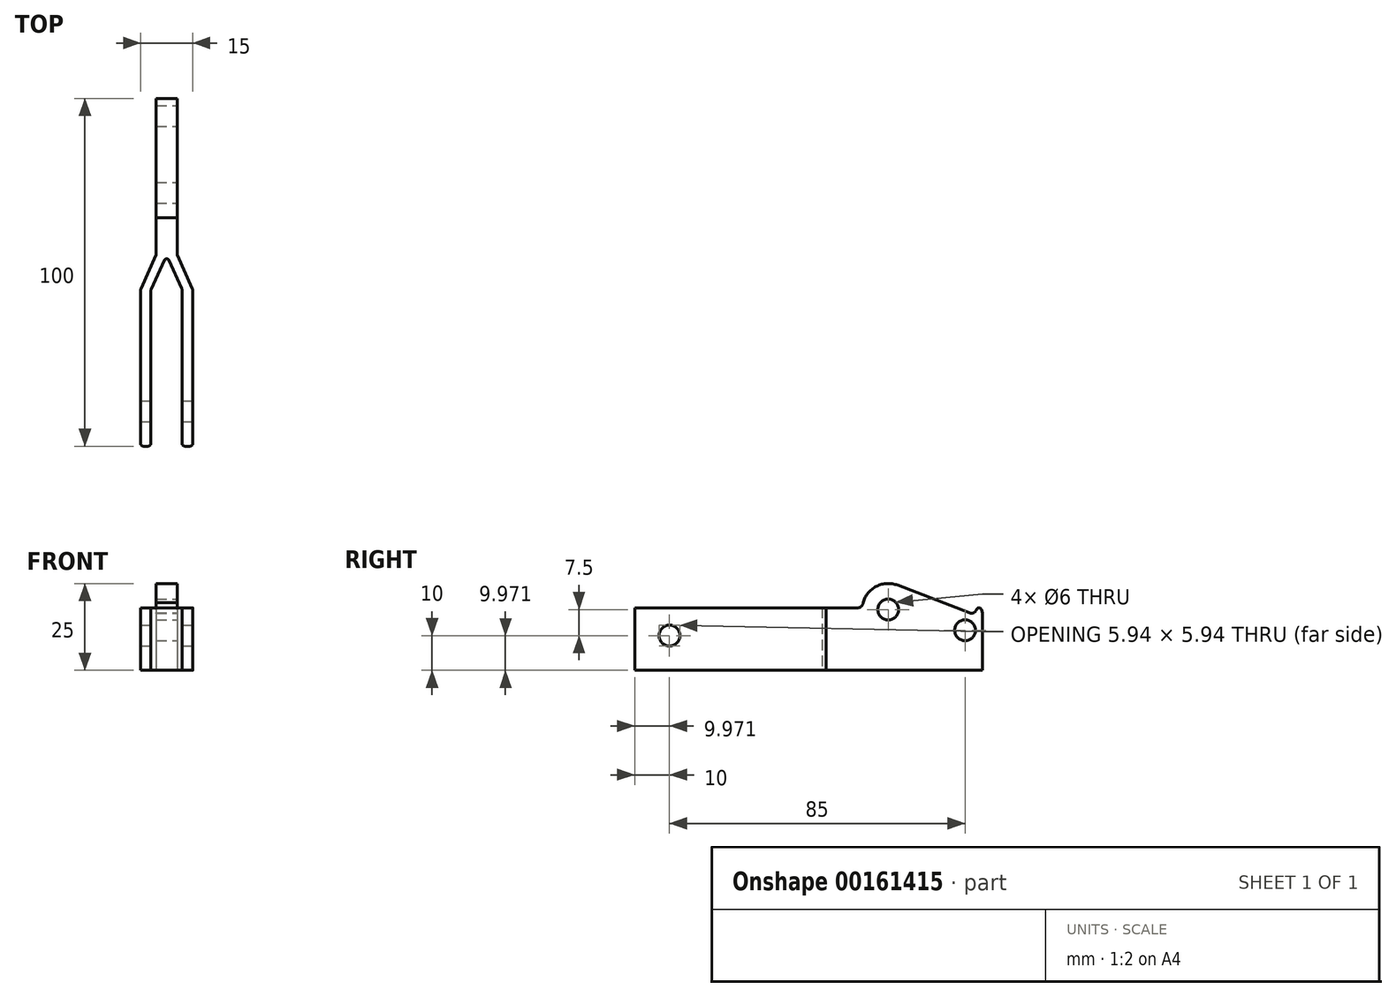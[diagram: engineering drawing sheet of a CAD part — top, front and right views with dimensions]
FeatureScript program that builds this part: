
annotation { "Feature Type Name" : "Feature", "Feature Type Description" : "" }
export const myFeature = defineFeature(function(context is Context, id is Id, definition is map)
    precondition{}
    {
        {
            var Q0;
            Q0=qCreatedBy(makeId("Top.planeOp"),FACE);
            var sketch = newSketch(context, id + "F0", { "sketchPlane" : qUnion([Q0])});
            skLineSegment(sketch, "E0.top", {"start": v(6.75, -22.5) * mm, "end": v(5.18, -22.5) * mm});
            skLineSegment(sketch, "E0.left", {"start": v(7.5, 22.18) * mm, "end": v(7.5, -21.75) * mm});
            skLineSegment(sketch, "E0.right", {"start": v(-7.5, 22.18) * mm, "end": v(-7.5, -21.75) * mm});
            skPoint(sketch, "E0.middle", {"position": v(0, 0) * mm});
            skLineSegment(sketch, "E1.left", {"start": v(-4.57, -21.75) * mm, "end": v(-4.57, 22.03) * mm});
            skLineSegment(sketch, "E1.right", {"start": v(4.43, -21.75) * mm, "end": v(4.43, 22.32) * mm});
            skLineSegment(sketch, "E2.trimOffspring", {"start": v(-5.32, -22.5) * mm, "end": v(-6.75, -22.5) * mm});
            skPoint(sketch, "E3", {"position": v(0, 32.5) * mm});
            skLineSegment(sketch, "E4", {"start": v(-4.43, 22.65) * mm, "end": v(-0.68, 30.98) * mm});
            skLineSegment(sketch, "E5", {"start": v(4.3, 22.94) * mm, "end": v(0.68, 30.98) * mm});
            skLineSegment(sketch, "E6", {"start": v(-7.37, 22.8) * mm, "end": v(-3, 32.5) * mm});
            skLineSegment(sketch, "E7", {"start": v(7.37, 22.8) * mm, "end": v(3, 32.5) * mm});
            skLineSegment(sketch, "E8.top", {"start": v(3, 77.5) * mm, "end": v(-3, 77.5) * mm});
            skLineSegment(sketch, "E8.left", {"start": v(3, 32.5) * mm, "end": v(3, 77.5) * mm});
            skLineSegment(sketch, "E8.right", {"start": v(-3, 32.5) * mm, "end": v(-3, 77.5) * mm});
            skPoint(sketch, "E8.middle", {"position": v(0, 55) * mm});
            skArc(sketch, "E9.filletArc", {"start": v(0.68, 30.98) * mm, "mid": v(0, 31.42) * mm, "end": v(-0.68, 30.98) * mm});
            skPoint(sketch, "E10.visualSharp", {"position": v(-4.57, -22.5) * mm});
            skArc(sketch, "E10.filletArc", {"start": v(-5.32, -22.5) * mm, "mid": v(-4.79, -22.28) * mm, "end": v(-4.57, -21.75) * mm});
            skPoint(sketch, "E11.visualSharp", {"position": v(-7.5, -22.5) * mm});
            skArc(sketch, "E11.filletArc", {"start": v(-7.5, -21.75) * mm, "mid": v(-7.28, -22.28) * mm, "end": v(-6.75, -22.5) * mm});
            skPoint(sketch, "E12.visualSharp", {"position": v(4.43, -22.5) * mm});
            skArc(sketch, "E12.filletArc", {"start": v(4.43, -21.75) * mm, "mid": v(4.65, -22.28) * mm, "end": v(5.18, -22.5) * mm});
            skPoint(sketch, "E13.visualSharp", {"position": v(7.5, -22.5) * mm});
            skArc(sketch, "E13.filletArc", {"start": v(6.75, -22.5) * mm, "mid": v(7.28, -22.28) * mm, "end": v(7.5, -21.75) * mm});
            skPoint(sketch, "E14.visualSharp", {"position": v(-4.57, 22.35) * mm});
            skArc(sketch, "E14.filletArc", {"start": v(-4.43, 22.65) * mm, "mid": v(-4.53, 22.35) * mm, "end": v(-4.57, 22.03) * mm});
            skPoint(sketch, "E15.visualSharp", {"position": v(4.43, 22.65) * mm});
            skArc(sketch, "E15.filletArc", {"start": v(4.43, 22.32) * mm, "mid": v(4.4, 22.64) * mm, "end": v(4.3, 22.94) * mm});
            skPoint(sketch, "E16.visualSharp", {"position": v(7.5, 22.5) * mm});
            skArc(sketch, "E16.filletArc", {"start": v(7.5, 22.18) * mm, "mid": v(7.47, 22.5) * mm, "end": v(7.37, 22.8) * mm});
            skPoint(sketch, "E17.visualSharp", {"position": v(-7.5, 22.5) * mm});
            skArc(sketch, "E17.filletArc", {"start": v(-7.37, 22.8) * mm, "mid": v(-7.47, 22.5) * mm, "end": v(-7.5, 22.18) * mm});
            skSolve(sketch);
        }
        {
            var Q0;
            Q0 = qSketchRegion(id + "F0", true);
            extrude(context, id + "F1", {"entities" : qUnion([Q0]), "depth" : 25 * mm});
        }
        {
            var Q0;
            Q0=makeQuery(id+"F1.opExtrude","SWEPT_FACE",FACE,{"disambiguationData":[OSD([sQuery(id+"F0.wireOp",EDGE,"E0.left")])]});
            var sketch = newSketch(context, id + "F2", { "sketchPlane" : qUnion([Q0])});
            skLineSegment(sketch, "E18.bottom", {"start": v(-21.83, 25) * mm, "end": v(43.17, 25) * mm});
            skLineSegment(sketch, "E18.top", {"start": v(-21.83, 18) * mm, "end": v(41.67, 18) * mm});
            skPoint(sketch, "E19.visualSharp", {"position": v(43.17, 18) * mm});
            skArc(sketch, "E19.filletArc", {"start": v(41.67, 18) * mm, "mid": v(42.73, 18.44) * mm, "end": v(43.17, 19.5) * mm});
            skArc(sketch, "E20", {"start": v(53.1, 24.5) * mm, "mid": v(46.73, 24.04) * mm, "end": v(43.02, 18.85) * mm});
            skArc(sketch, "E21", {"start": v(77.21, 17.48) * mm, "mid": v(76.5, 18) * mm, "end": v(75.79, 17.48) * mm});
            skLineSegment(sketch, "E22", {"start": v(77.5, 16.58) * mm, "end": v(77.21, 17.48) * mm});
            skPoint(sketch, "E23.orphan", {"position": v(76.5, 19.73) * mm});
            skLineSegment(sketch, "E24", {"start": v(73.82, 16.53) * mm, "end": v(53.1, 24.5) * mm});
            skPoint(sketch, "E25.visualSharp", {"position": v(75.3, 15.96) * mm});
            skArc(sketch, "E25.filletArc", {"start": v(73.82, 16.53) * mm, "mid": v(75, 16.58) * mm, "end": v(75.79, 17.48) * mm});
            skPoint(sketch, "E26.orphan", {"position": v(77.5, 18) * mm});
            skLineSegment(sketch, "E27", {"start": v(77.5, 16.58) * mm, "end": v(77.5, 25) * mm});
            skLineSegment(sketch, "E28", {"start": v(-21.75, 25) * mm, "end": v(77.5, 25) * mm});
            skCircle(sketch, "E29", {"center": v(50.4, 17.5) * mm, "radius": 3 * mm});
            skLineSegment(sketch, "E30", {"start": v(-21.75, 25) * mm, "end": v(-23.69, 25) * mm});
            skLineSegment(sketch, "E31", {"start": v(-23.69, 25) * mm, "end": v(-23.69, 18) * mm});
            skLineSegment(sketch, "E32", {"start": v(-23.69, 18) * mm, "end": v(-21.83, 18) * mm});
            skCircle(sketch, "E33", {"center": v(-12.5, 10) * mm, "radius": 3 * mm});
            skCircle(sketch, "E34", {"center": v(72.5, 11.53) * mm, "radius": 3 * mm});
            skSolve(sketch);
        }
        {
            var Q0;
            Q0 = qSketchRegion(id + "F2", true);
            extrude(context, id + "F3", {"entities" : qUnion([Q0]), "operationType" : NewBodyOperationType.REMOVE, "oppositeDirection" : true, "depth" : 15 * mm});
        }
    });
